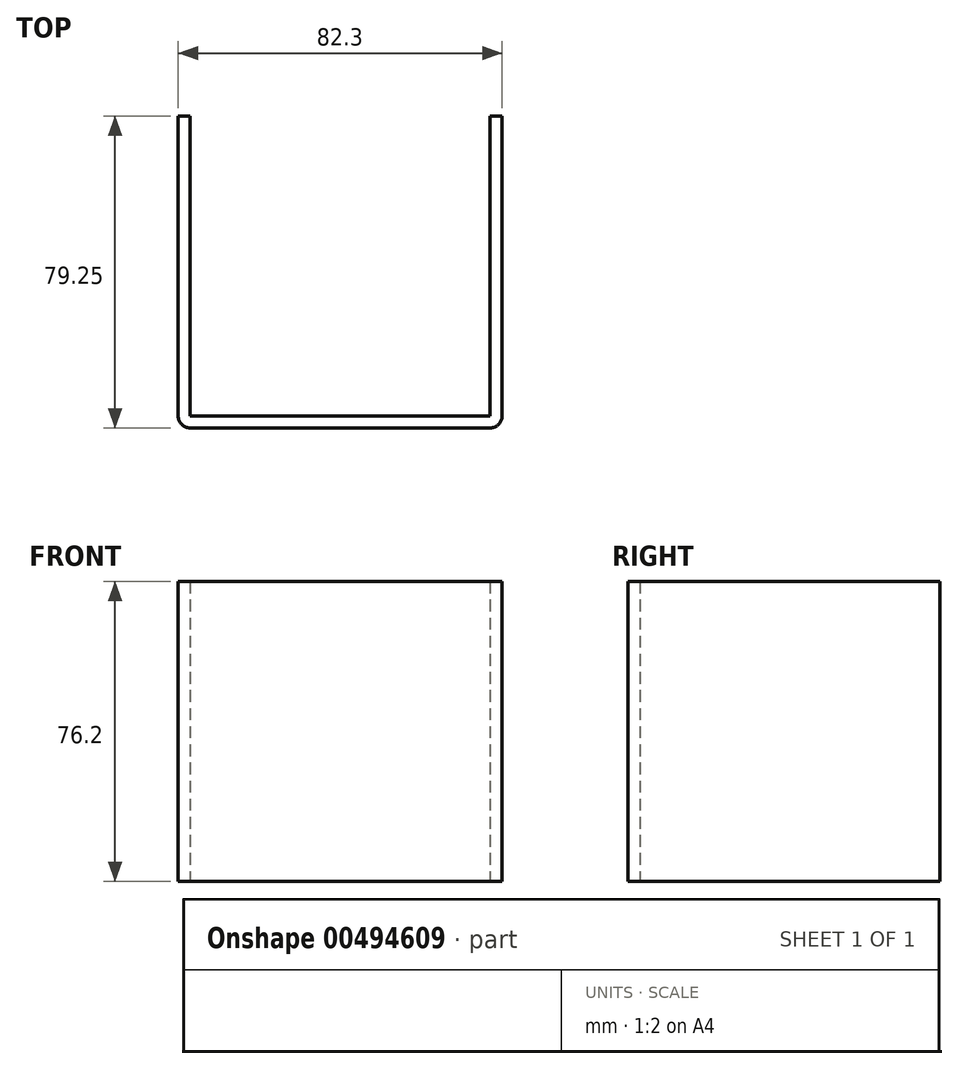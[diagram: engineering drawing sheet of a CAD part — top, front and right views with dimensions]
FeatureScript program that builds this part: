
annotation { "Feature Type Name" : "Feature", "Feature Type Description" : "" }
export const myFeature = defineFeature(function(context is Context, id is Id, definition is map)
    precondition{}
    {
        {
            var Q0;
            Q0=qCreatedBy(makeId("Top.planeOp"),FACE);
            var sketch = newSketch(context, id + "F0", { "sketchPlane" : qUnion([Q0])});
            skLineSegment(sketch, "E0", {"start": v(-38.1, 0) * mm, "end": v(38.1, 0) * mm, "construction": true});
            skPoint(sketch, "E1", {"position": v(0, 0) * mm});
            skLineSegment(sketch, "E2", {"start": v(-38.1, 0) * mm, "end": v(-38.1, -76.2) * mm});
            skLineSegment(sketch, "E3", {"start": v(-38.1, -76.2) * mm, "end": v(38.1, -76.2) * mm});
            skLineSegment(sketch, "E4", {"start": v(38.1, -76.2) * mm, "end": v(38.1, 0) * mm});
            skLineSegment(sketch, "E5.0", {"start": v(41.15, -76.2) * mm, "end": v(41.15, 0) * mm});
            skLineSegment(sketch, "E5.1", {"start": v(-38.1, -79.25) * mm, "end": v(38.1, -79.25) * mm});
            skLineSegment(sketch, "E5.2", {"start": v(-41.15, 0) * mm, "end": v(-41.15, -76.2) * mm});
            skLineSegment(sketch, "E6", {"start": v(-38.1, 0) * mm, "end": v(-41.15, 0) * mm});
            skLineSegment(sketch, "E7", {"start": v(41.15, 0) * mm, "end": v(38.1, 0) * mm});
            skPoint(sketch, "E8.visualSharp", {"position": v(-41.15, -79.25) * mm});
            skArc(sketch, "E8.filletArc", {"start": v(-41.15, -76.2) * mm, "mid": v(-40.26, -78.36) * mm, "end": v(-38.1, -79.25) * mm});
            skPoint(sketch, "E9.visualSharp", {"position": v(41.15, -79.25) * mm});
            skArc(sketch, "E9.filletArc", {"start": v(38.1, -79.25) * mm, "mid": v(40.26, -78.36) * mm, "end": v(41.15, -76.2) * mm});
            skSolve(sketch);
        }
        {
            var Q0;
            Q0=makeQuery(id+"F0.imprint","IMPRINT",FACE,{"disambiguationData":[TD([[makeQuery(id+"F0.imprint","IMPRINT",EDGE,{"derivedFrom":sQuery(id+"F0.wireOp",EDGE,"E2")}),-1.0]])]});
            extrude(context, id + "F1", {"entities" : qUnion([Q0]), "depth" : 76.2 * mm});
        }
    });
